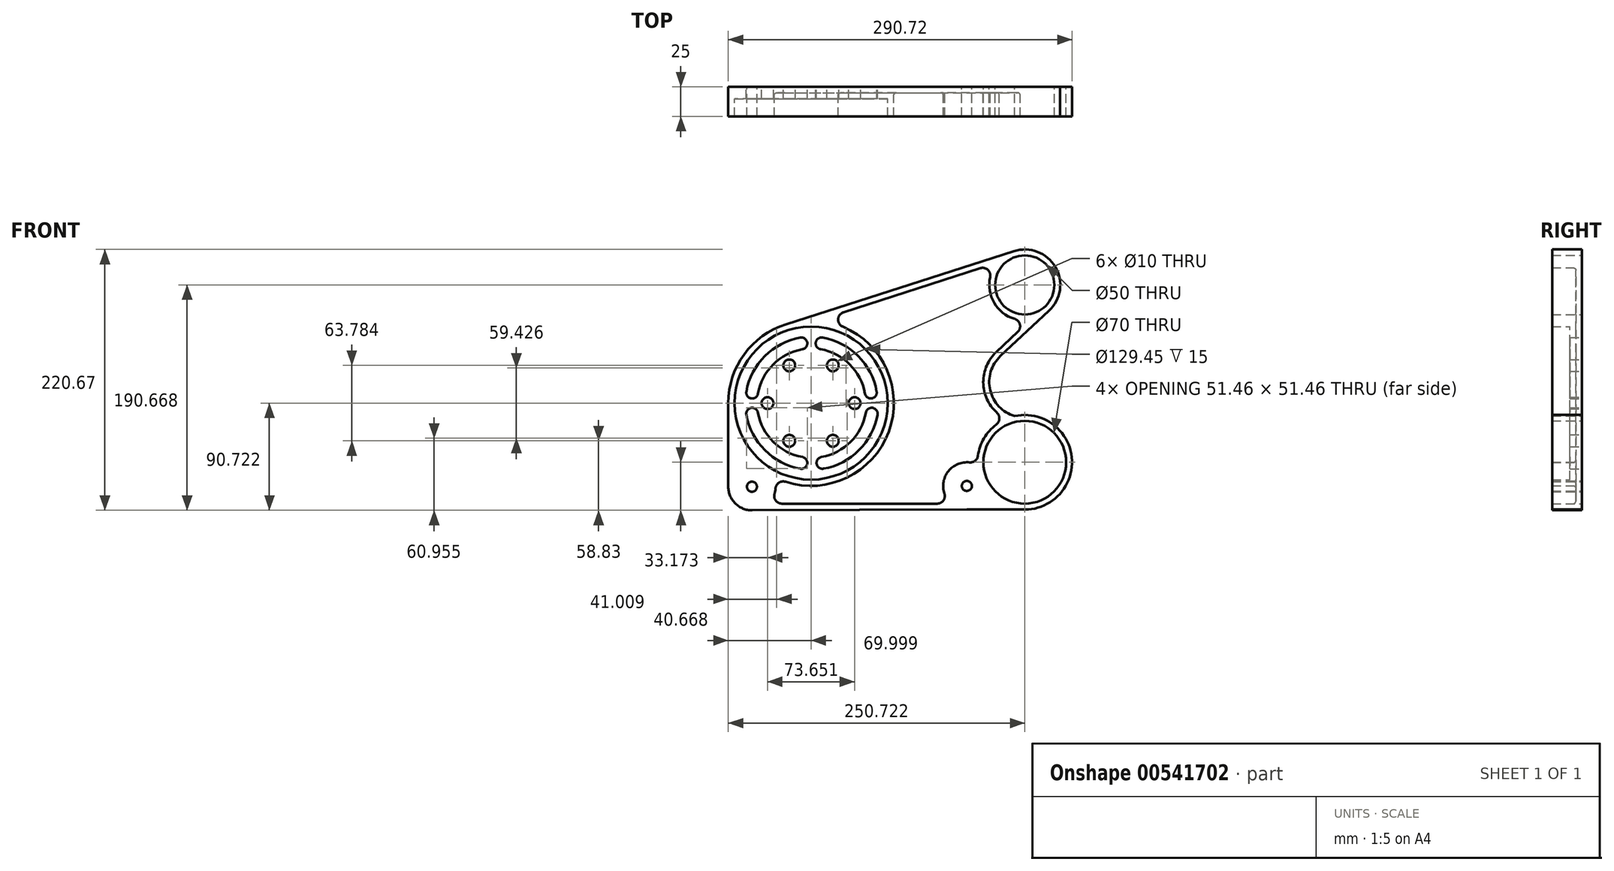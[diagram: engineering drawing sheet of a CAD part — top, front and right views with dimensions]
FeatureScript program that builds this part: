
annotation { "Feature Type Name" : "Feature", "Feature Type Description" : "" }
export const myFeature = defineFeature(function(context is Context, id is Id, definition is map)
    precondition{}
    {
        {
            var Q0;
            Q0=qCreatedBy(makeId("Front.planeOp"),FACE);
            var sketch = newSketch(context, id + "F0", { "sketchPlane" : qUnion([Q0])});
            skCircle(sketch, "E0", {"center": v(-9.22, 8.55) * mm, "radius": 64.73 * mm});
            skCircle(sketch, "E1", {"center": v(-46.05, 8.55) * mm, "radius": 5 * mm});
            skCircle(sketch, "E2.1.0", {"center": v(-27.63, -23.34) * mm, "radius": 5 * mm});
            skCircle(sketch, "E2.2.0", {"center": v(9.2, -23.34) * mm, "radius": 5 * mm});
            skCircle(sketch, "E2.3.0", {"center": v(27.6, 8.55) * mm, "radius": 5 * mm});
            skCircle(sketch, "E2.4.0", {"center": v(9.2, 40.44) * mm, "radius": 5 * mm});
            skCircle(sketch, "E2.5.0", {"center": v(-27.63, 40.44) * mm, "radius": 5 * mm});
            skArc(sketch, "E3.0", {"start": v(-30.8, -58.04) * mm, "mid": v(56.44, -15.7) * mm, "end": v(17.66, 73.18) * mm});
            skArc(sketch, "E4", {"start": v(36.37, 16.6) * mm, "mid": v(42.17, 12.54) * mm, "end": v(46.22, 18.33) * mm});
            skArc(sketch, "E5", {"start": v(0.55, 64) * mm, "mid": v(-5.24, 59.94) * mm, "end": v(-1.18, 54.15) * mm});
            skArc(sketch, "E6", {"start": v(0.55, 64) * mm, "mid": v(30.59, 48.36) * mm, "end": v(46.22, 18.33) * mm});
            skArc(sketch, "E7", {"start": v(-1.18, 54.15) * mm, "mid": v(23.52, 41.29) * mm, "end": v(36.37, 16.6) * mm});
            skArc(sketch, "E8.MirrorCS", {"start": v(-18.27, 63.94) * mm, "mid": v(-12.48, 59.88) * mm, "end": v(-16.54, 54.1) * mm});
            skArc(sketch, "E9.MirrorCS", {"start": v(-18.27, 63.94) * mm, "mid": v(-48.3, 48.3) * mm, "end": v(-63.94, 18.27) * mm});
            skArc(sketch, "E10.MirrorCS", {"start": v(-16.54, 54.1) * mm, "mid": v(-41.24, 41.24) * mm, "end": v(-54.1, 16.54) * mm});
            skArc(sketch, "E11.MirrorCS", {"start": v(-54.1, 16.54) * mm, "mid": v(-59.88, 12.48) * mm, "end": v(-63.94, 18.27) * mm});
            skArc(sketch, "E12.MirrorCS", {"start": v(-54.1, 0.46) * mm, "mid": v(-59.88, 4.51) * mm, "end": v(-63.94, -1.28) * mm});
            skArc(sketch, "E13.MirrorCS", {"start": v(-18.27, -46.94) * mm, "mid": v(-48.3, -31.31) * mm, "end": v(-63.94, -1.28) * mm});
            skArc(sketch, "E14.MirrorCS", {"start": v(-16.54, -37.1) * mm, "mid": v(-41.24, -24.24) * mm, "end": v(-54.1, 0.46) * mm});
            skArc(sketch, "E15.MirrorCS", {"start": v(-18.27, -46.94) * mm, "mid": v(-12.48, -42.89) * mm, "end": v(-16.54, -37.1) * mm});
            skArc(sketch, "E16.MirrorCS", {"start": v(1.28, -46.94) * mm, "mid": v(-4.51, -42.89) * mm, "end": v(-0.46, -37.1) * mm});
            skArc(sketch, "E17.MirrorCS", {"start": v(1.28, -46.94) * mm, "mid": v(31.31, -31.31) * mm, "end": v(46.94, -1.28) * mm});
            skArc(sketch, "E18.MirrorCS", {"start": v(37.1, 0.46) * mm, "mid": v(42.89, 4.51) * mm, "end": v(46.94, -1.28) * mm});
            skArc(sketch, "E19.MirrorCS", {"start": v(-0.46, -37.1) * mm, "mid": v(24.24, -24.24) * mm, "end": v(37.1, 0.46) * mm});
            skCircle(sketch, "E20", {"center": v(171.5, -41.5) * mm, "radius": 35 * mm});
            skCircle(sketch, "E21", {"center": v(171.5, 108.5) * mm, "radius": 25 * mm});
            skArc(sketch, "E22.0", {"start": v(142.22, 115.04) * mm, "mid": v(145.63, 93.3) * mm, "end": v(162.96, 79.74) * mm});
            skArc(sketch, "E23.0", {"start": v(147.44, -9.55) * mm, "mid": v(137, -21.25) * mm, "end": v(131.87, -36.05) * mm});
            skArc(sketch, "E24.0", {"start": v(-79.22, -62.17) * mm, "mid": v(-73.34, -76.34) * mm, "end": v(-59.15, -82.17) * mm});
            skLineSegment(sketch, "E25", {"start": v(-30.6, 75.2) * mm, "end": v(162.34, 137.07) * mm});
            skLineSegment(sketch, "E26", {"start": v(18.16, 85.37) * mm, "end": v(133.89, 122.65) * mm});
            skLineSegment(sketch, "E27", {"start": v(-79.22, 8.55) * mm, "end": v(-79.22, -62.17) * mm});
            skLineSegment(sketch, "E28", {"start": v(-59.15, -82.17) * mm, "end": v(122.5, -81.5) * mm});
            skLineSegment(sketch, "E29", {"start": v(-33.9, -76.5) * mm, "end": v(97.4, -76.5) * mm});
            skArc(sketch, "E30.trimOffspring", {"start": v(-40.11, -68.08) * mm, "mid": v(-39.58, -65.92) * mm, "end": v(-39.28, -63.72) * mm});
            skArc(sketch, "E31.trimOffspring", {"start": v(-30.6, 75.2) * mm, "mid": v(-65.77, 49.8) * mm, "end": v(-79.22, 8.55) * mm});
            skLineSegment(sketch, "E32", {"start": v(122.5, -81.5) * mm, "end": v(171.5, -81.5) * mm});
            skArc(sketch, "E33", {"start": v(150.95, 48.32) * mm, "mid": v(142.22, 19.45) * mm, "end": v(163, -2.42) * mm});
            skArc(sketch, "E34.0", {"start": v(147.54, 51.98) * mm, "mid": v(136.41, 26.14) * mm, "end": v(147.9, 0.46) * mm});
            skLineSegment(sketch, "E35", {"start": v(165.54, 68.76) * mm, "end": v(147.54, 51.98) * mm});
            skPoint(sketch, "E35.startSnap0", {"position": v(188.55, 83.81) * mm});
            skLineSegment(sketch, "E36", {"start": v(191.96, 86.56) * mm, "end": v(150.95, 48.32) * mm});
            skPoint(sketch, "E37.orphan", {"position": v(188.55, 90.21) * mm});
            skArc(sketch, "E38.trimOffspring", {"start": v(191.96, 86.56) * mm, "mid": v(197.38, 123.67) * mm, "end": v(162.34, 137.07) * mm});
            skArc(sketch, "E39.trimOffspring", {"start": v(124.72, -41.62) * mm, "mid": v(106.92, -48.96) * mm, "end": v(103.56, -67.92) * mm});
            skArc(sketch, "E40.trimOffspring", {"start": v(171.5, -81.5) * mm, "mid": v(211.27, -37.22) * mm, "end": v(163, -2.42) * mm});
            skArc(sketch, "E41", {"start": v(97.4, -76.5) * mm, "mid": v(102.68, -73.79) * mm, "end": v(103.56, -67.92) * mm});
            skArc(sketch, "E42", {"start": v(124.72, -41.62) * mm, "mid": v(129.43, -40.3) * mm, "end": v(131.87, -36.05) * mm});
            skArc(sketch, "E43", {"start": v(147.44, -9.55) * mm, "mid": v(150.02, -4.65) * mm, "end": v(147.9, 0.46) * mm});
            skArc(sketch, "E44", {"start": v(165.54, 68.76) * mm, "mid": v(167.43, 75) * mm, "end": v(162.96, 79.74) * mm});
            skArc(sketch, "E45", {"start": v(142.22, 115.04) * mm, "mid": v(140.26, 121.26) * mm, "end": v(133.89, 122.65) * mm});
            skArc(sketch, "E46", {"start": v(18.16, 85.37) * mm, "mid": v(13.66, 79.45) * mm, "end": v(17.66, 73.18) * mm});
            skArc(sketch, "E47", {"start": v(-30.8, -58.04) * mm, "mid": v(-36.42, -58.82) * mm, "end": v(-39.28, -63.72) * mm});
            skArc(sketch, "E48", {"start": v(-40.11, -68.08) * mm, "mid": v(-39.14, -73.86) * mm, "end": v(-33.9, -76.5) * mm});
            skCircle(sketch, "E49", {"center": v(-59.22, -62.17) * mm, "radius": 4.25 * mm});
            skCircle(sketch, "E50", {"center": v(122.5, -61.5) * mm, "radius": 4.25 * mm});
            skSolve(sketch);
        }
        {
            var Q0;
            Q0=makeQuery(id+"F0.imprint","IMPRINT",FACE,{"disambiguationData":[TD([[makeQuery(id+"F0.imprint","IMPRINT",EDGE,{"derivedFrom":sQuery(id+"F0.wireOp",EDGE,"E0")}),-1.0]])]});
            extrude(context, id + "F1", {"entities" : qUnion([Q0]), "depth" : 25 * mm, "offsetDistance" : 25 * mm});
        }
        {
            var Q0;
            Q0=makeQuery(id+"F0.imprint","IMPRINT",FACE,{"disambiguationData":[TD([[makeQuery(id+"F0.imprint","IMPRINT",EDGE,{"derivedFrom":sQuery(id+"F0.wireOp",EDGE,"E3.0")}),-1.0]])]});
            extrude(context, id + "F2", {"entities" : qUnion([Q0]), "operationType" : NewBodyOperationType.ADD, "depth" : 5 * mm, "offsetDistance" : 25 * mm});
        }
        {
            var Q0;
            Q0=makeQuery(id+"F0.imprint","IMPRINT",FACE,{"disambiguationData":[TD([[makeQuery(id+"F0.imprint","IMPRINT",EDGE,{"derivedFrom":sQuery(id+"F0.wireOp",EDGE,"E0")}),1.0]])]});
            extrude(context, id + "F3", {"entities" : qUnion([Q0]), "operationType" : NewBodyOperationType.ADD, "depth" : 10 * mm, "offsetDistance" : 25 * mm});
        }
        {
            var Q0;
            Q0=makeQuery(id+"F2.opExtrude","CAP_FACE",FACE,{"disambiguationData":[OSD([sQuery(id+"F0.wireOp",EDGE,"E3.0"),sQuery(id+"F0.wireOp",EDGE,"E22.0"),sQuery(id+"F0.wireOp",EDGE,"E23.0"),sQuery(id+"F0.wireOp",EDGE,"E26"),sQuery(id+"F0.wireOp",EDGE,"E29"),sQuery(id+"F0.wireOp",EDGE,"E30.trimOffspring"),sQuery(id+"F0.wireOp",EDGE,"E34.0"),sQuery(id+"F0.wireOp",EDGE,"E35"),sQuery(id+"F0.wireOp",EDGE,"E39.trimOffspring"),sQuery(id+"F0.wireOp",EDGE,"E41"),sQuery(id+"F0.wireOp",EDGE,"E42"),sQuery(id+"F0.wireOp",EDGE,"E43"),sQuery(id+"F0.wireOp",EDGE,"E44"),sQuery(id+"F0.wireOp",EDGE,"E45"),sQuery(id+"F0.wireOp",EDGE,"E46"),sQuery(id+"F0.wireOp",EDGE,"E47"),sQuery(id+"F0.wireOp",EDGE,"E48")])],"isStart":false});
            fillet(context, id + "F4", {"entities" : qUnion([Q0]), "radius" : 2 * mm, "tangentPropagation" : true, "allowEdgeOverflow" : false});
        }
    });
